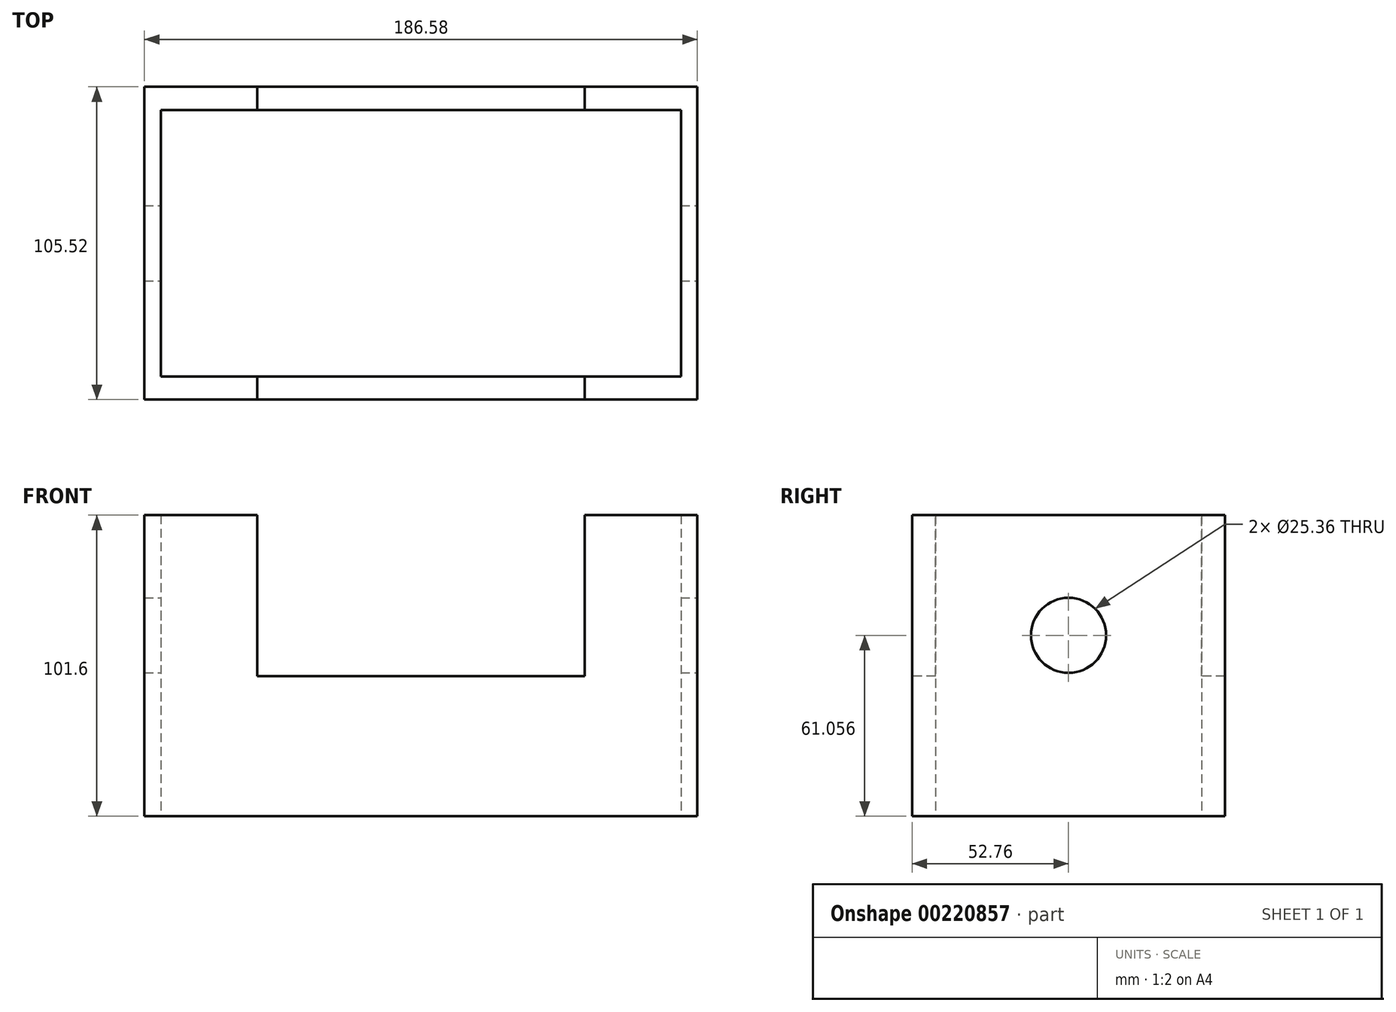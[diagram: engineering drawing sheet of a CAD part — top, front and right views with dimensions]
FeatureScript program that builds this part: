
annotation { "Feature Type Name" : "Feature", "Feature Type Description" : "" }
export const myFeature = defineFeature(function(context is Context, id is Id, definition is map)
    precondition{}
    {
        {
            var Q0;
            Q0=qCreatedBy(makeId("Top.planeOp"),FACE);
            var sketch = newSketch(context, id + "F0", { "sketchPlane" : qUnion([Q0])});
            skLineSegment(sketch, "E0.bottom", {"start": v(87.75, -44.91) * mm, "end": v(-87.75, -44.91) * mm});
            skLineSegment(sketch, "E0.top", {"start": v(87.75, 44.91) * mm, "end": v(-87.75, 44.91) * mm});
            skLineSegment(sketch, "E0.left", {"start": v(87.75, -44.91) * mm, "end": v(87.75, 44.91) * mm});
            skLineSegment(sketch, "E0.right", {"start": v(-87.75, -44.91) * mm, "end": v(-87.75, 44.91) * mm});
            skPoint(sketch, "E0.middle", {"position": v(0, 0) * mm});
            skLineSegment(sketch, "E1.bottom", {"start": v(93.29, -52.76) * mm, "end": v(-93.29, -52.76) * mm});
            skLineSegment(sketch, "E1.top", {"start": v(93.29, 52.76) * mm, "end": v(-93.29, 52.76) * mm});
            skLineSegment(sketch, "E1.left", {"start": v(93.29, -52.76) * mm, "end": v(93.29, 52.76) * mm});
            skLineSegment(sketch, "E1.right", {"start": v(-93.29, -52.76) * mm, "end": v(-93.29, 52.76) * mm});
            skSolve(sketch);
        }
        {
            var Q0;
            Q0=makeQuery(id+"F0.imprint","IMPRINT",FACE,{"disambiguationData":[TD([[makeQuery(id+"F0.imprint","IMPRINT",EDGE,{"derivedFrom":sQuery(id+"F0.wireOp",EDGE,"E0.bottom")}),1.0]])]});
            extrude(context, id + "F1", {"entities" : qUnion([Q0]), "depth" : 101.6 * mm});
        }
        {
            var Q0;
            Q0=makeQuery(id+"F1.opExtrude","SWEPT_FACE",FACE,{"disambiguationData":[OSD([sQuery(id+"F0.wireOp",EDGE,"E1.bottom")])]});
            var sketch = newSketch(context, id + "F2", { "sketchPlane" : qUnion([Q0])});
            skLineSegment(sketch, "E2.bottom", {"start": v(55.23, 47.32) * mm, "end": v(-55.23, 47.32) * mm});
            skLineSegment(sketch, "E2.top", {"start": v(55.23, 102.81) * mm, "end": v(-55.23, 102.81) * mm});
            skLineSegment(sketch, "E2.left", {"start": v(55.23, 47.32) * mm, "end": v(55.23, 102.81) * mm});
            skLineSegment(sketch, "E2.right", {"start": v(-55.23, 47.32) * mm, "end": v(-55.23, 102.81) * mm});
            skPoint(sketch, "E2.middle", {"position": v(0, 75.06) * mm});
            skSolve(sketch);
        }
        {
            var Q0;
            Q0 = qSketchRegion(id + "F2", true);
            extrude(context, id + "F3", {"entities" : qUnion([Q0]), "operationType" : NewBodyOperationType.REMOVE, "oppositeDirection" : true, "depth" : 115.82 * mm});
        }
        {
            var Q0;
            Q0=makeQuery(id+"F1.opExtrude","SWEPT_FACE",FACE,{"disambiguationData":[OSD([sQuery(id+"F0.wireOp",EDGE,"E1.left")])]});
            var sketch = newSketch(context, id + "F4", { "sketchPlane" : qUnion([Q0])});
            skCircle(sketch, "E3", {"center": v(0, 61.06) * mm, "radius": 12.68 * mm});
            skSolve(sketch);
        }
        {
            var Q0;
            Q0 = qSketchRegion(id + "F4", true);
            extrude(context, id + "F5", {"entities" : qUnion([Q0]), "operationType" : NewBodyOperationType.REMOVE, "oppositeDirection" : true, "depth" : 207.26 * mm});
        }
    });
